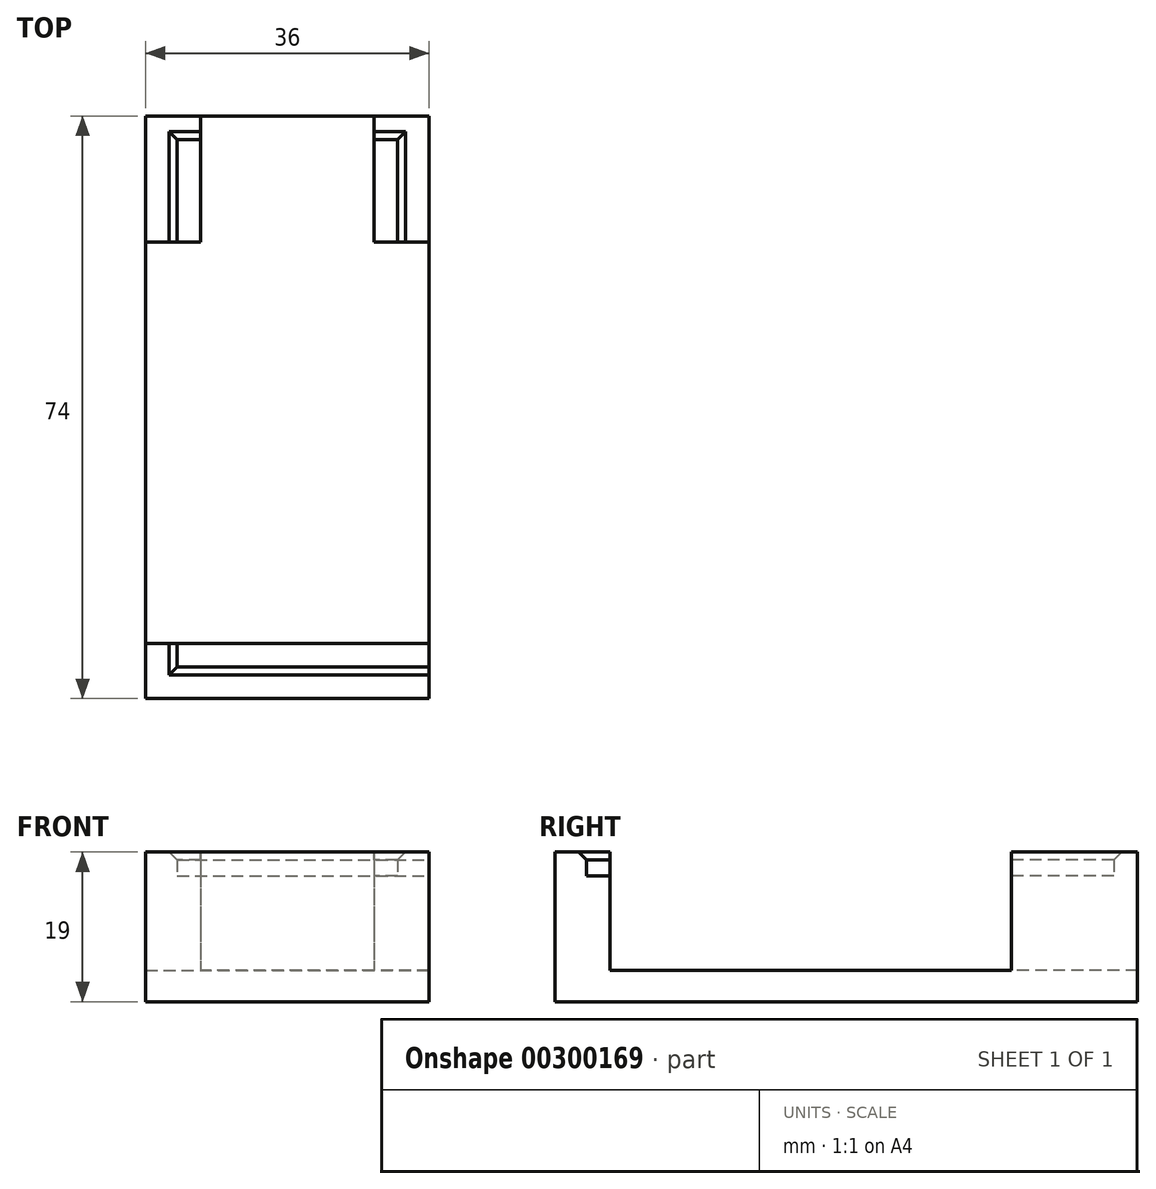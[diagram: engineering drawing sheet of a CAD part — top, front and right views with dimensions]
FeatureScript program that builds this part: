
annotation { "Feature Type Name" : "Feature", "Feature Type Description" : "" }
export const myFeature = defineFeature(function(context is Context, id is Id, definition is map)
    precondition{}
    {
        {
            var Q0;
            Q0=qCreatedBy(makeId("Top.planeOp"),FACE);
            var sketch = newSketch(context, id + "F0", { "sketchPlane" : qUnion([Q0])});
            skLineSegment(sketch, "E0.bottom", {"start": v(18, 37) * mm, "end": v(-18, 37) * mm});
            skLineSegment(sketch, "E0.top", {"start": v(18, -37) * mm, "end": v(-18, -37) * mm});
            skLineSegment(sketch, "E0.left", {"start": v(18, 37) * mm, "end": v(18, -37) * mm});
            skLineSegment(sketch, "E0.right", {"start": v(-18, 37) * mm, "end": v(-18, -37) * mm});
            skPoint(sketch, "E0.middle", {"position": v(0, 0) * mm});
            skSolve(sketch);
        }
        {
            var Q0;
            Q0 = qSketchRegion(id + "F0", true);
            extrude(context, id + "F1", {"entities" : qUnion([Q0]), "depth" : 4 * mm});
        }
        {
            var Q0;
            Q0=makeQuery(id+"F1.opExtrude","CAP_FACE",FACE,{"disambiguationData":[OSD([sQuery(id+"F0.wireOp",EDGE,"E0.bottom"),sQuery(id+"F0.wireOp",EDGE,"E0.top"),sQuery(id+"F0.wireOp",EDGE,"E0.left"),sQuery(id+"F0.wireOp",EDGE,"E0.right")])],"isStart":false});
            var sketch = newSketch(context, id + "F2", { "sketchPlane" : qUnion([Q0])});
            skLineSegment(sketch, "E1.bottom", {"start": v(-18, 37) * mm, "end": v(-11, 37) * mm});
            skLineSegment(sketch, "E1.top", {"start": v(-18, 21) * mm, "end": v(-11, 21) * mm});
            skLineSegment(sketch, "E1.left", {"start": v(-18, 37) * mm, "end": v(-18, 21) * mm});
            skLineSegment(sketch, "E1.right", {"start": v(-11, 37) * mm, "end": v(-11, 21) * mm});
            skLineSegment(sketch, "E2.bottom", {"start": v(18, 37) * mm, "end": v(11, 37) * mm});
            skLineSegment(sketch, "E2.top", {"start": v(18, 21) * mm, "end": v(11, 21) * mm});
            skLineSegment(sketch, "E2.left", {"start": v(18, 37) * mm, "end": v(18, 21) * mm});
            skLineSegment(sketch, "E2.right", {"start": v(11, 37) * mm, "end": v(11, 21) * mm});
            skLineSegment(sketch, "E3.bottom", {"start": v(-18, -37) * mm, "end": v(18, -37) * mm});
            skLineSegment(sketch, "E3.top", {"start": v(-18, -30) * mm, "end": v(18, -30) * mm});
            skLineSegment(sketch, "E3.left", {"start": v(-18, -37) * mm, "end": v(-18, -30) * mm});
            skLineSegment(sketch, "E3.right", {"start": v(18, -37) * mm, "end": v(18, -30) * mm});
            skLineSegment(sketch, "E4", {"start": v(-11, 34) * mm, "end": v(-14, 34) * mm});
            skLineSegment(sketch, "E5", {"start": v(-14, 34) * mm, "end": v(-14, 21) * mm});
            skLineSegment(sketch, "E6", {"start": v(11, 34) * mm, "end": v(14, 34) * mm});
            skLineSegment(sketch, "E7", {"start": v(14, 34) * mm, "end": v(14, 21) * mm});
            skLineSegment(sketch, "E8", {"start": v(-14, -30) * mm, "end": v(-14, -33) * mm});
            skLineSegment(sketch, "E9", {"start": v(-14, -33) * mm, "end": v(18, -33) * mm});
            skLineSegment(sketch, "E10", {"start": v(-14, 21) * mm, "end": v(-14, -30) * mm, "construction": true});
            skSolve(sketch);
        }
        {
            var Q0;
            {var subQ4=sQuery(id+"F2.wireOp",EDGE,"E4");Q0=makeQuery(id+"F2.imprint","IMPRINT",FACE,{"disambiguationData":[TD([[makeQuery(id+"F2.imprint","IMPRINT",EDGE,{"derivedFrom":subQ4}),1.0]])]});}
            var Q1;
            {var subQ4=sQuery(id+"F2.wireOp",EDGE,"E6");Q1=makeQuery(id+"F2.imprint","IMPRINT",FACE,{"disambiguationData":[TD([[makeQuery(id+"F2.imprint","IMPRINT",EDGE,{"derivedFrom":subQ4}),-1.0]])]});}
            var Q2;
            {var subQ3=sQuery(id+"F2.wireOp",EDGE,"E8");Q2=makeQuery(id+"F2.imprint","IMPRINT",FACE,{"disambiguationData":[TD([[makeQuery(id+"F2.imprint","IMPRINT",EDGE,{"derivedFrom":subQ3}),1.0]])]});}
            extrude(context, id + "F3", {"entities" : qUnion([Q0, Q1, Q2]), "operationType" : NewBodyOperationType.ADD, "depth" : 12 * mm});
        }
        {
            var Q0;
            {var subQ1=sQuery(id+"F2.wireOp",EDGE,"E1.bottom");Q0=makeQuery(id+"F2.imprint","IMPRINT",FACE,{"disambiguationData":[TD([[makeQuery(id+"F2.imprint","IMPRINT",EDGE,{"derivedFrom":subQ1}),1.0]])]});}
            var Q1;
            {var subQ1=sQuery(id+"F2.wireOp",EDGE,"E2.bottom");Q1=makeQuery(id+"F2.imprint","IMPRINT",FACE,{"disambiguationData":[TD([[makeQuery(id+"F2.imprint","IMPRINT",EDGE,{"derivedFrom":subQ1}),1.0]])]});}
            var Q2;
            {var subQ4=sQuery(id+"F2.wireOp",EDGE,"E3.bottom");Q2=makeQuery(id+"F2.imprint","IMPRINT",FACE,{"disambiguationData":[TD([[makeQuery(id+"F2.imprint","IMPRINT",EDGE,{"derivedFrom":subQ4}),-1.0]])]});}
            extrude(context, id + "F4", {"entities" : qUnion([Q0, Q1, Q2]), "operationType" : NewBodyOperationType.ADD, "depth" : 15 * mm});
        }
        {
            var Q0;
            Q0=makeQuery(id+"F4.opExtrude","CAP_EDGE",EDGE,{"disambiguationData":[OSD([sQuery(id+"F2.wireOp",EDGE,"E5")])],"isStart":false});
            var Q1;
            Q1=makeQuery(id+"F4.opExtrude","CAP_EDGE",EDGE,{"disambiguationData":[OSD([sQuery(id+"F2.wireOp",EDGE,"E4")])],"isStart":false});
            var Q2;
            Q2=makeQuery(id+"F4.opExtrude","CAP_EDGE",EDGE,{"disambiguationData":[OSD([sQuery(id+"F2.wireOp",EDGE,"E6")])],"isStart":false});
            var Q3;
            Q3=makeQuery(id+"F4.opExtrude","CAP_EDGE",EDGE,{"disambiguationData":[OSD([sQuery(id+"F2.wireOp",EDGE,"E7")])],"isStart":false});
            var Q4;
            Q4=makeQuery(id+"F4.opExtrude","CAP_EDGE",EDGE,{"disambiguationData":[OSD([sQuery(id+"F2.wireOp",EDGE,"E9")])],"isStart":false});
            var Q5;
            Q5=makeQuery(id+"F4.opExtrude","CAP_EDGE",EDGE,{"disambiguationData":[OSD([sQuery(id+"F2.wireOp",EDGE,"E8")])],"isStart":false});
            chamfer(context, id + "F5", {"entities" : qUnion([Q0, Q1, Q2, Q3, Q4, Q5]), "width" : 1 * mm, "tangentPropagation" : true});
        }
    });
